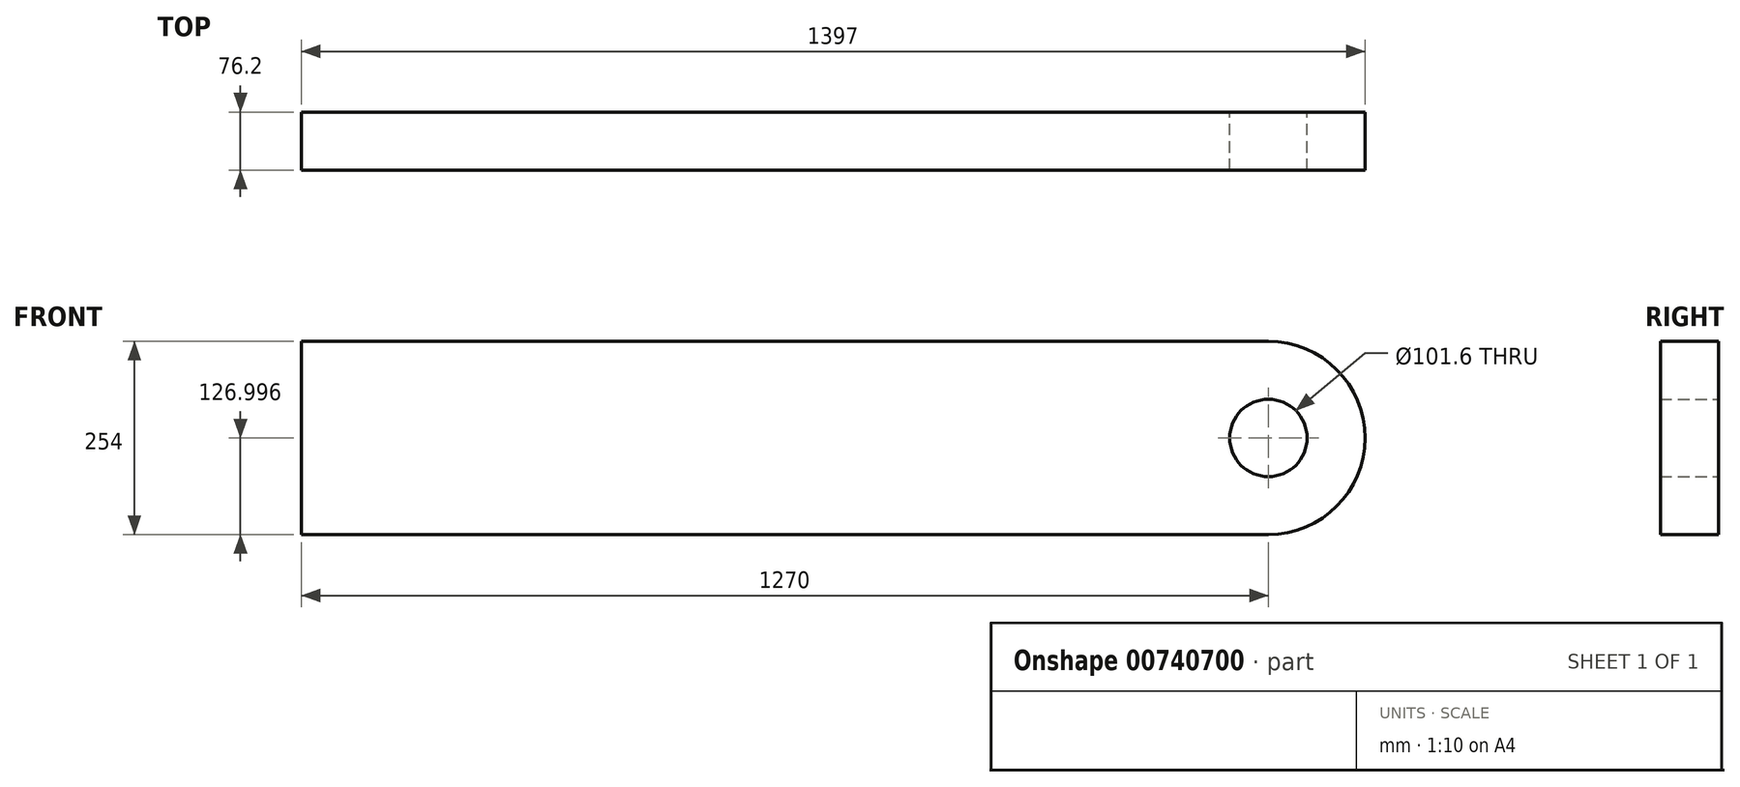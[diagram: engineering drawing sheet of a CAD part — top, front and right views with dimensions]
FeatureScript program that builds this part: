
annotation { "Feature Type Name" : "Feature", "Feature Type Description" : "" }
export const myFeature = defineFeature(function(context is Context, id is Id, definition is map)
    precondition{}
    {
        {
            var Q0;
            Q0=qCreatedBy(makeId("Front.planeOp"),FACE);
            var sketch = newSketch(context, id + "F0", { "sketchPlane" : qUnion([Q0])});
            skLineSegment(sketch, "E0", {"start": v(-1250.02, 243.45) * mm, "end": v(19.98, 243.45) * mm});
            skLineSegment(sketch, "E1", {"start": v(-1250.02, -10.55) * mm, "end": v(19.98, -10.55) * mm});
            skArc(sketch, "E2", {"start": v(19.98, -10.55) * mm, "mid": v(146.98, 116.45) * mm, "end": v(19.98, 243.45) * mm});
            skLineSegment(sketch, "E3", {"start": v(-1250.02, 243.45) * mm, "end": v(-1250.02, -10.55) * mm});
            skCircle(sketch, "E4", {"center": v(19.98, 116.45) * mm, "radius": 6.15 * mm});
            skCircle(sketch, "E5", {"center": v(19.98, 116.45) * mm, "radius": 50.8 * mm});
            skSolve(sketch);
        }
        {
            var Q0;
            Q0 = qSketchRegion(id + "F0", true);
            extrude(context, id + "F1", {"entities" : qUnion([Q0]), "depth" : 76.2 * mm, "offsetDistance" : 25.4 * mm});
        }
    });
